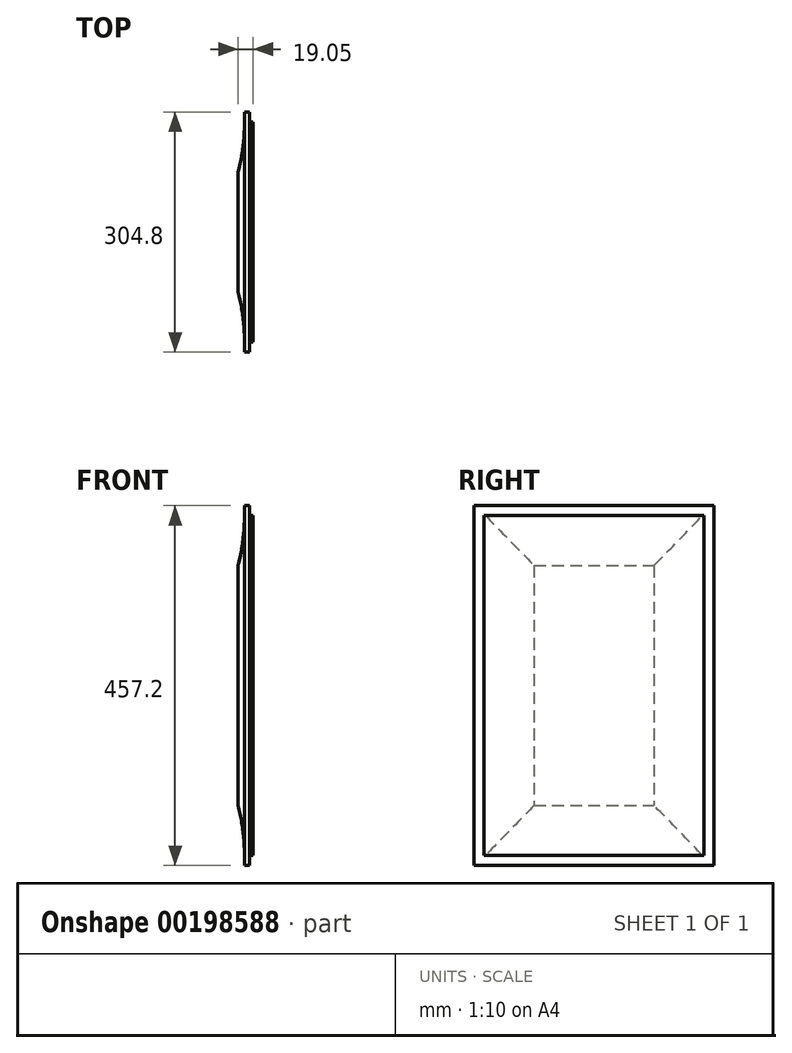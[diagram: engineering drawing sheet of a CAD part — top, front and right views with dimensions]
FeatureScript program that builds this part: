
annotation { "Feature Type Name" : "Feature", "Feature Type Description" : "" }
export const myFeature = defineFeature(function(context is Context, id is Id, definition is map)
    precondition{}
    {
        {
            var Q0;
            Q0=qCreatedBy(makeId("Right.planeOp"),FACE);
            var sketch = newSketch(context, id + "F0", { "sketchPlane" : qUnion([Q0])});
            skLineSegment(sketch, "E0", {"start": v(300.81, 0) * mm, "end": v(-461.19, 0) * mm, "construction": true});
            skLineSegment(sketch, "E1.bottom", {"start": v(0, 0) * mm, "end": v(-304.8, 0) * mm});
            skLineSegment(sketch, "E1.top", {"start": v(0, 457.2) * mm, "end": v(-304.8, 457.2) * mm});
            skLineSegment(sketch, "E1.left", {"start": v(0, 0) * mm, "end": v(0, 457.2) * mm});
            skLineSegment(sketch, "E1.right", {"start": v(-304.8, 0) * mm, "end": v(-304.8, 457.2) * mm});
            skSolve(sketch);
        }
        {
            var Q0;
            Q0 = qSketchRegion(id + "F0", true);
            extrude(context, id + "F1", {"entities" : qUnion([Q0]), "depth" : 19.05 * mm});
        }
        {
            var Q0;
            Q0=makeQuery(id+"F1.opExtrude","SWEPT_FACE",FACE,{"disambiguationData":[OSD([sQuery(id+"F0.wireOp",EDGE,"E1.bottom")])]});
            var sketch = newSketch(context, id + "F2", { "sketchPlane" : qUnion([Q0])});
            skPoint(sketch, "E2.startSnap0", {"position": v(0, 152.4) * mm});
            skLineSegment(sketch, "E3", {"start": v(9.53, 0) * mm, "end": v(7.94, 0) * mm});
            skLineSegment(sketch, "E4", {"start": v(7.94, 0) * mm, "end": v(14.29, 0) * mm});
            skLineSegment(sketch, "E5", {"start": v(14.29, 0) * mm, "end": v(14.29, 12.7) * mm});
            skLineSegment(sketch, "E6", {"start": v(14.29, 12.7) * mm, "end": v(19.05, 12.7) * mm});
            skLineSegment(sketch, "E7", {"start": v(19.05, 12.7) * mm, "end": v(19.05, 0) * mm});
            skLineSegment(sketch, "E8", {"start": v(19.05, 0) * mm, "end": v(14.29, 0) * mm});
            skLineSegment(sketch, "E9", {"start": v(0, 0) * mm, "end": v(0, 76.2) * mm});
            skLineSegment(sketch, "E10", {"start": v(7.94, 0) * mm, "end": v(7.94, 12.7) * mm});
            skArc(sketch, "E11", {"start": v(7.94, 12.7) * mm, "mid": v(6.05, 44.7) * mm, "end": v(0, 76.2) * mm});
            skLineSegment(sketch, "E12.MirrorCS", {"start": v(19.05, 290.24) * mm, "end": v(19.05, 254.06) * mm});
            skLineSegment(sketch, "E13.MirrorCS", {"start": v(19.05, 290.24) * mm, "end": v(19.05, 304.8) * mm});
            skLineSegment(sketch, "E14.MirrorCS", {"start": v(0, 304.8) * mm, "end": v(0, 228.6) * mm});
            skLineSegment(sketch, "E15.MirrorCS", {"start": v(7.94, 304.8) * mm, "end": v(7.94, 292.1) * mm});
            skArc(sketch, "E16.MirrorCS", {"start": v(7.94, 292.1) * mm, "mid": v(6.05, 260.1) * mm, "end": v(0, 228.6) * mm});
            skLineSegment(sketch, "E17", {"start": v(19.05, 304.8) * mm, "end": v(14.29, 304.8) * mm});
            skLineSegment(sketch, "E18.top", {"start": v(19.05, 292.1) * mm, "end": v(14.29, 292.1) * mm});
            skLineSegment(sketch, "E18.left", {"start": v(19.05, 304.8) * mm, "end": v(19.05, 292.1) * mm});
            skLineSegment(sketch, "E18.right", {"start": v(14.29, 304.8) * mm, "end": v(14.29, 292.1) * mm});
            skSolve(sketch);
        }
        {
            var Q0;
            Q0 = qSketchRegion(id + "F2", true);
            var Q1;
            {var subQ0=sQuery(id+"F2.wireOp",EDGE,"E9");Q1=makeQuery(id+"F2.imprint","IMPRINT",FACE,{"disambiguationData":[TD([[makeQuery(id+"F2.imprint","IMPRINT",EDGE,{"derivedFrom":subQ0}),-1.0]])]});}
            var Q2;
            {var subQ0=sQuery(id+"F2.wireOp",EDGE,"E14.MirrorCS");Q2=makeQuery(id+"F2.imprint","IMPRINT",FACE,{"disambiguationData":[TD([[makeQuery(id+"F2.imprint","IMPRINT",EDGE,{"derivedFrom":subQ0}),-1.0]])]});}
            extrude(context, id + "F3", {"entities" : qUnion([Q0, Q1, Q2]), "operationType" : NewBodyOperationType.REMOVE, "endBound" : BoundingType.THROUGH_ALL, "oppositeDirection" : true, "depth" : 25.4 * mm});
        }
        {
            var Q0;
            Q0=makeQuery(id+"F1.opExtrude","SWEPT_FACE",FACE,{"disambiguationData":[OSD([sQuery(id+"F0.wireOp",EDGE,"E1.left")])]});
            var sketch = newSketch(context, id + "F4", { "sketchPlane" : qUnion([Q0])});
            skLineSegment(sketch, "E19", {"start": v(23.07, 228.6) * mm, "end": v(-43.92, 228.6) * mm});
            skPoint(sketch, "E19.startSnap0", {"position": v(-7.94, 228.6) * mm});
            skLineSegment(sketch, "E20", {"start": v(-7.94, 457.2) * mm, "end": v(-7.94, 444.5) * mm});
            skLineSegment(sketch, "E21", {"start": v(0, 457.2) * mm, "end": v(0, 381) * mm});
            skArc(sketch, "E22", {"start": v(-7.94, 444.5) * mm, "mid": v(-5.95, 412.5) * mm, "end": v(0, 381) * mm});
            skLineSegment(sketch, "E23", {"start": v(-7.94, 457.2) * mm, "end": v(0, 457.2) * mm});
            skLineSegment(sketch, "E24.MirrorCS", {"start": v(-7.94, 0) * mm, "end": v(0, 0) * mm});
            skLineSegment(sketch, "E25.MirrorCS", {"start": v(0, 0) * mm, "end": v(0, 76.2) * mm});
            skArc(sketch, "E26.MirrorCS", {"start": v(-7.94, 12.7) * mm, "mid": v(-5.95, 44.7) * mm, "end": v(0, 76.2) * mm});
            skLineSegment(sketch, "E27.MirrorCS", {"start": v(-7.94, 0) * mm, "end": v(-7.94, 12.7) * mm});
            skLineSegment(sketch, "E28.bottom", {"start": v(-14.29, 457.2) * mm, "end": v(-19.05, 457.2) * mm});
            skLineSegment(sketch, "E28.top", {"start": v(-14.29, 444.5) * mm, "end": v(-19.05, 444.5) * mm});
            skLineSegment(sketch, "E28.left", {"start": v(-14.29, 457.2) * mm, "end": v(-14.29, 444.5) * mm});
            skLineSegment(sketch, "E28.right", {"start": v(-19.05, 457.2) * mm, "end": v(-19.05, 444.5) * mm});
            skLineSegment(sketch, "E29.MirrorCS", {"start": v(-14.29, 12.7) * mm, "end": v(-19.05, 12.7) * mm});
            skLineSegment(sketch, "E30.MirrorCS", {"start": v(-14.29, 0) * mm, "end": v(-19.05, 0) * mm});
            skLineSegment(sketch, "E31.MirrorCS", {"start": v(-19.05, 0) * mm, "end": v(-19.05, 12.7) * mm});
            skLineSegment(sketch, "E32.MirrorCS", {"start": v(-14.29, 0) * mm, "end": v(-14.29, 12.7) * mm});
            skSolve(sketch);
        }
        {
            var Q0;
            Q0 = qSketchRegion(id + "F4", true);
            extrude(context, id + "F5", {"entities" : qUnion([Q0]), "operationType" : NewBodyOperationType.REMOVE, "endBound" : BoundingType.THROUGH_ALL, "oppositeDirection" : true, "depth" : 25.4 * mm});
        }
    });
